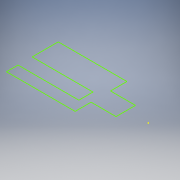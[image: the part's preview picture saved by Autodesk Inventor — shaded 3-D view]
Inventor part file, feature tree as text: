
AUTODESK INVENTOR PART (.ipt)
format: ipt  version: 2016 (Build 200138000, 138)  size: 81,408 bytes
history: native  units: mm
features: sketch x1
ambient origin geometry x8: Origin, YZ Plane, XZ Plane, XY Plane, X Axis, Y Axis, Z Axis, Center Point
feature tree (1):
  sketch  "Sketch1"
